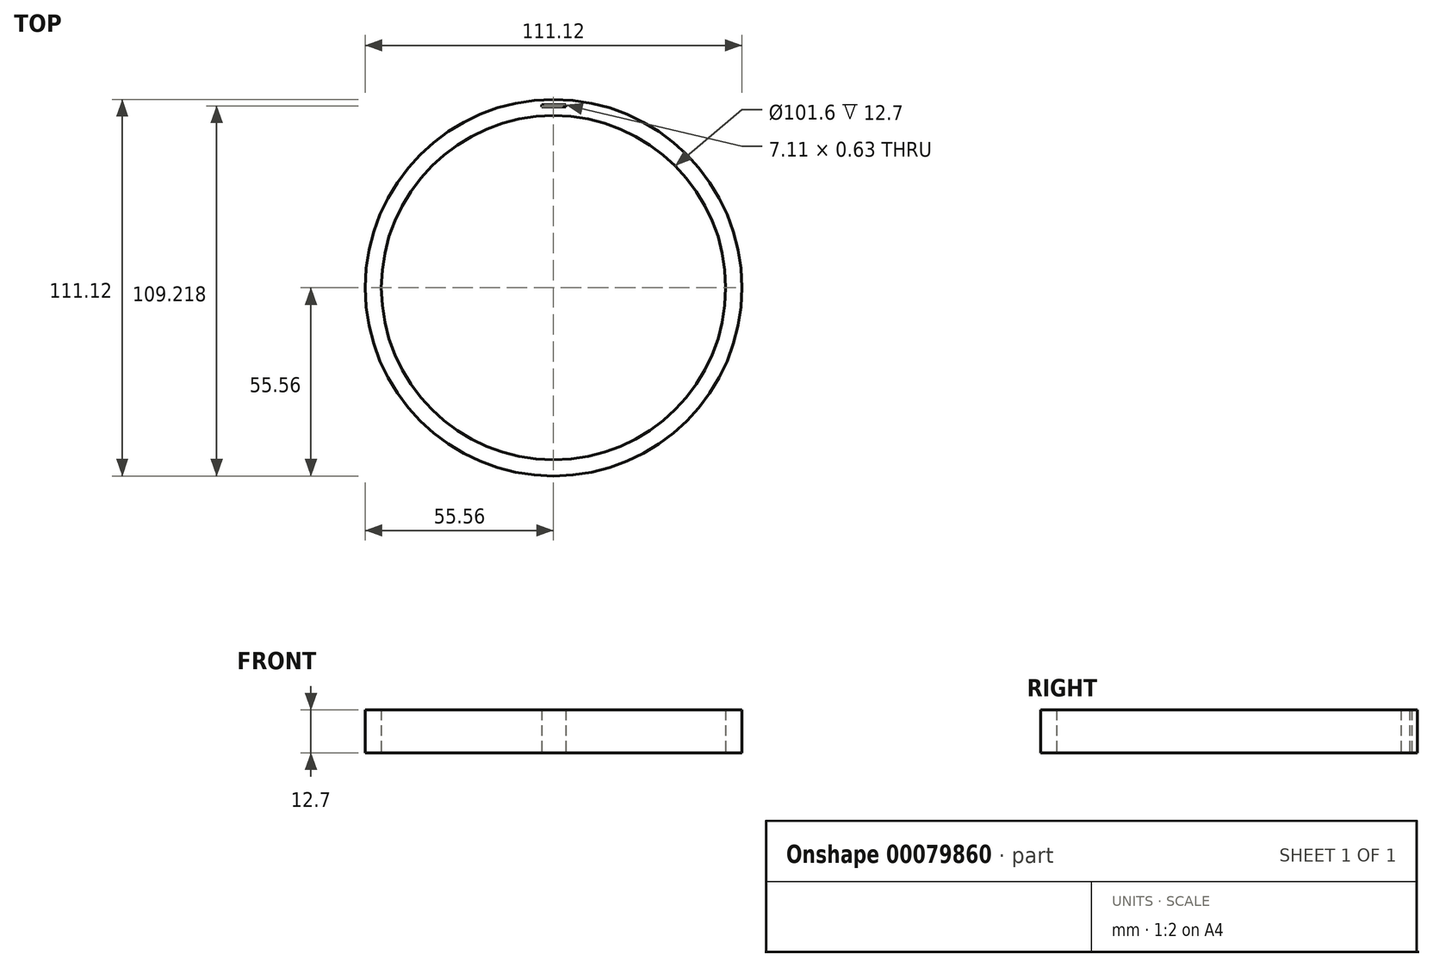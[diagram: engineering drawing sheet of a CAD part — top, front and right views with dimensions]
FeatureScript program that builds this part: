
annotation { "Feature Type Name" : "Feature", "Feature Type Description" : "" }
export const myFeature = defineFeature(function(context is Context, id is Id, definition is map)
    precondition{}
    {
        {
            var Q0;
            Q0=qCreatedBy(makeId("Top.planeOp"),FACE);
            var sketch = newSketch(context, id + "F0", { "sketchPlane" : qUnion([Q0])});
            skCircle(sketch, "E0", {"center": v(0, 0) * mm, "radius": 50.8 * mm});
            skCircle(sketch, "E1", {"center": v(0, 0) * mm, "radius": 55.56 * mm});
            skPoint(sketch, "E2.orphan", {"position": v(0, 33.94) * mm});
            skLineSegment(sketch, "E3", {"start": v(0, 50.8) * mm, "end": v(0, 55.56) * mm});
            skPoint(sketch, "E4", {"position": v(0, 53.98) * mm});
            skLineSegment(sketch, "E5", {"start": v(-3.56, 53.98) * mm, "end": v(3.56, 53.98) * mm});
            skLineSegment(sketch, "E6", {"start": v(-3.56, 53.98) * mm, "end": v(-3.56, 53.34) * mm});
            skLineSegment(sketch, "E7", {"start": v(-3.56, 53.34) * mm, "end": v(3.56, 53.34) * mm});
            skLineSegment(sketch, "E8", {"start": v(3.56, 53.34) * mm, "end": v(3.56, 53.98) * mm});
            skSolve(sketch);
        }
        {
            var Q0;
            Q0=makeQuery(id+"F0.imprint","IMPRINT",FACE,{"disambiguationData":[TD([[makeQuery(id+"F0.imprint","IMPRINT",EDGE,{"derivedFrom":sQuery(id+"F0.wireOp",EDGE,"E0")}),-1.0]])]});
            extrude(context, id + "F1", {"entities" : qUnion([Q0]), "depth" : 12.7 * mm});
        }
    });
